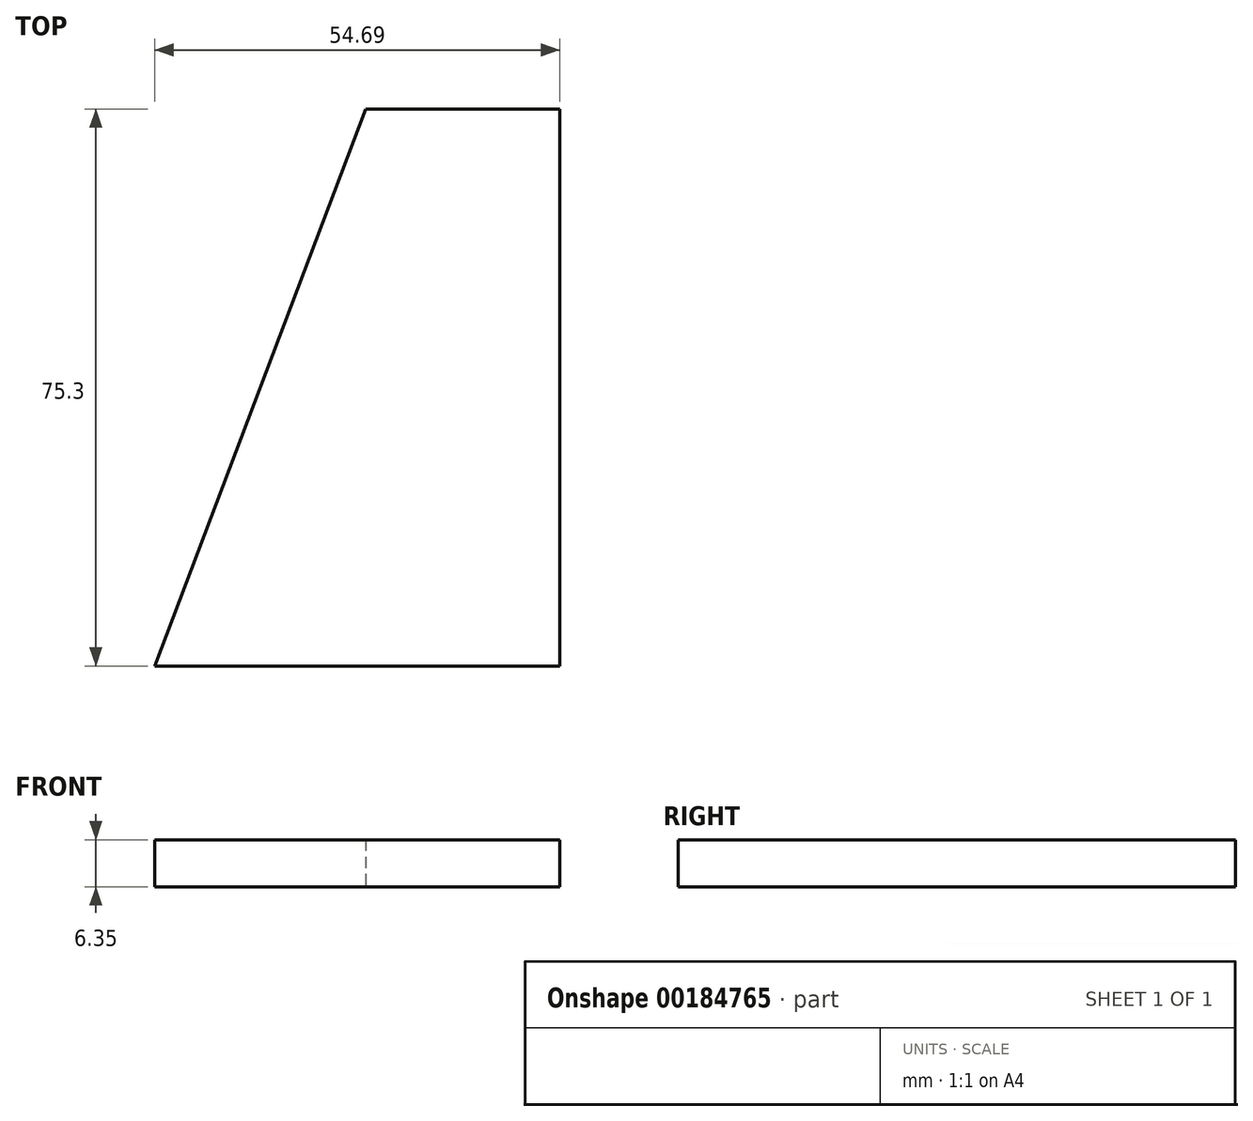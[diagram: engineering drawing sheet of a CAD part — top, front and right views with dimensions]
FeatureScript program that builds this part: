
annotation { "Feature Type Name" : "Feature", "Feature Type Description" : "" }
export const myFeature = defineFeature(function(context is Context, id is Id, definition is map)
    precondition{}
    {
        {
            var Q0;
            Q0=qCreatedBy(makeId("Top.planeOp"),FACE);
            var sketch = newSketch(context, id + "F0", { "sketchPlane" : qUnion([Q0])});
            skLineSegment(sketch, "E0", {"start": v(33.07, 43.63) * mm, "end": v(33.07, -31.67) * mm});
            skLineSegment(sketch, "E1", {"start": v(33.07, -31.67) * mm, "end": v(-21.62, -31.67) * mm});
            skLineSegment(sketch, "E2", {"start": v(-21.62, -31.67) * mm, "end": v(6.87, 43.63) * mm});
            skLineSegment(sketch, "E3", {"start": v(6.87, 43.63) * mm, "end": v(33.07, 43.63) * mm});
            skSolve(sketch);
        }
        {
            var Q0;
            Q0 = qSketchRegion(id + "F0", true);
            extrude(context, id + "F1", {"entities" : qUnion([Q0]), "depth" : 6.35 * mm});
        }
    });
